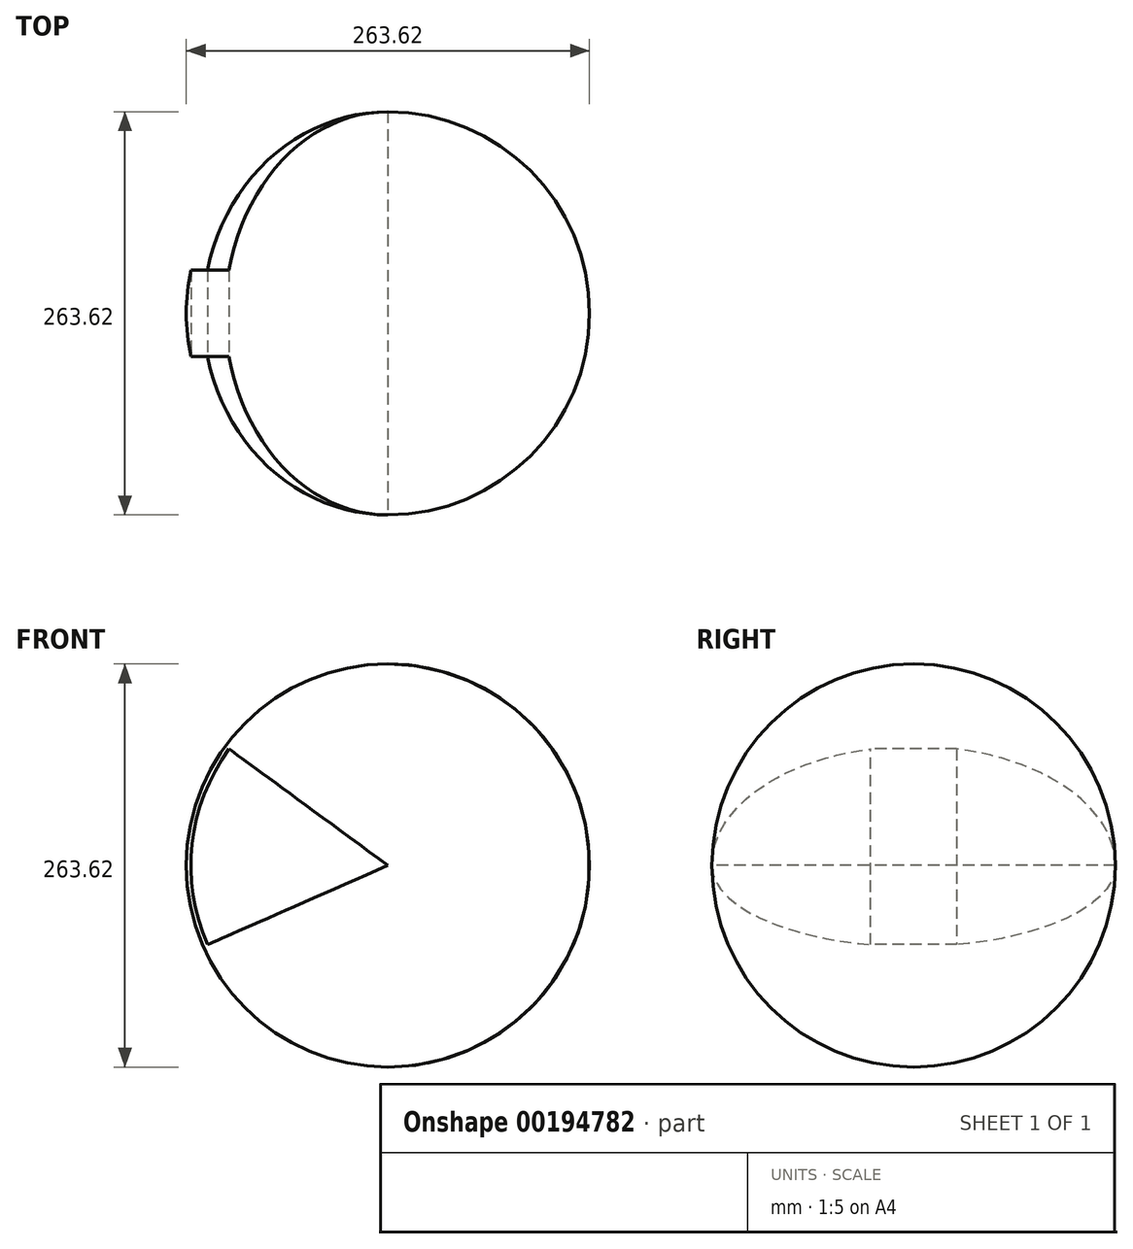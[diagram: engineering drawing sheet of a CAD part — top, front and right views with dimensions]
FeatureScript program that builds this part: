
annotation { "Feature Type Name" : "Feature", "Feature Type Description" : "" }
export const myFeature = defineFeature(function(context is Context, id is Id, definition is map)
    precondition{}
    {
        {
            var Q0;
            Q0=qCreatedBy(makeId("Front.planeOp"),FACE);
            var sketch = newSketch(context, id + "F0", { "sketchPlane" : qUnion([Q0])});
            skArc(sketch, "E0", {"start": v(0, -131.8) * mm, "mid": v(131.8, 0) * mm, "end": v(0, 131.8) * mm});
            skLineSegment(sketch, "E1", {"start": v(0, 131.8) * mm, "end": v(0, -131.8) * mm});
            skLineSegment(sketch, "E2", {"start": v(0, -131.8) * mm, "end": v(0, 131.8) * mm});
            skSolve(sketch);
        }
        {
            var Q0;
            Q0=makeQuery(id+"F0.imprint","IMPRINT",FACE,{"disambiguationData":[TD([[makeQuery(id+"F0.imprint","IMPRINT",EDGE,{"derivedFrom":sQuery(id+"F0.wireOp",EDGE,"E0")}),1.0]])]});
            var Q1;
            Q1=sQuery(id+"F0.wireOp",EDGE,"E2");
            revolve(context, id + "F1", {"entities" : qUnion([Q0]), "axis" : qUnion([Q1]), "revolveType" : RevolveType.FULL});
        }
        {
            var Q0;
            Q0=qCreatedBy(makeId("Front.planeOp"),FACE);
            var sketch = newSketch(context, id + "F2", { "sketchPlane" : qUnion([Q0])});
            skLineSegment(sketch, "E3", {"start": v(0, 0) * mm, "end": v(-106.61, 78.32) * mm});
            skLineSegment(sketch, "E4", {"start": v(0, 0) * mm, "end": v(-118.76, -52.12) * mm});
            skLineSegment(sketch, "E5", {"start": v(0, 0) * mm, "end": v(-131.65, 14.54) * mm});
            skArc(sketch, "E6", {"start": v(-103.76, 76.23) * mm, "mid": v(-127.97, 14.14) * mm, "end": v(-117.9, -51.74) * mm});
            skSolve(sketch);
        }
        {
            var Q0;
            Q0 = qSketchRegion(id + "F2", true);
            extrude(context, id + "F3", {"entities" : qUnion([Q0]), "operationType" : NewBodyOperationType.REMOVE, "oppositeDirection" : true, "depth" : 233.68 * mm});
        }
        {
            var Q0;
            Q0 = qSketchRegion(id + "F2", true);
            extrude(context, id + "F4", {"entities" : qUnion([Q0]), "operationType" : NewBodyOperationType.REMOVE, "depth" : 241.3 * mm});
        }
    });
